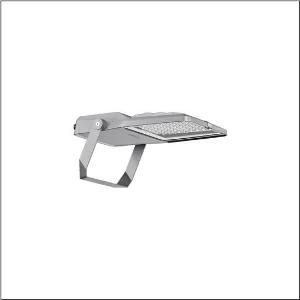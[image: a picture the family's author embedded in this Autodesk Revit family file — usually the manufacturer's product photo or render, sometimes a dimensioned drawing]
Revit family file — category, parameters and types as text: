
# Revit family: floodlight_fl_21_iq_mini___pl52_5xa7772d2d1a_b3d3
name_source: partatom
category: Lighting Fixtures
units: mm (PartAtom-declared; Revit-internal decimal feet)

## family parameters
Cut with Voids When Loaded = No
Host = Face
Light Source = No
Part Type = Normal
Room Calculation Point = No
Round Connector Dimension = Use Diameter
Shared = No

## types (1)
- --- (1 x LED, 17830 lm, 143 W, 3000K)
    Apparent Load = 143 VA
    CIE Flux Codes = 26 60 98 100 100
    Color Rendering = 70
    Color Temperature = 3000K
    Default Elevation = 1800 mm
    Description = Floodlight FL 21 iQ mini, floodlight, primary light control with lens, of PMMA, primary optical cover: protective disc, of toughened safety glass, transparent, light distribution: PL52, light emission: direct distribution, installation type: surface-mounted, LED, High Power LED, rated luminous flux: 17.830lm, luminous efficacy: 125lm/W, light colour: 730, colour temperature: 3000K, control: Street-Remote, Auto-Match, Temp-Guard, Night-Set, Smart-Wire, Desk-Remote (wireless, voltage-free reading and setting of iQ features in the workshop via application-optimized NFC function/RFID function), optimised constant luminous flux control (CLO 2.0), with terminal, 6-pole, mains connection: 220..240V, AC, 50/60Hz, start of lifetime: 143W, end of service life: 152W, reduction: 61W, luminaire housing, of diecast aluminium, powder-coated, Siteco® metallic grey (DB 702S), corrosivity category C5 mid according to DIN EN ISO 12944, sealing non-destructively replaceable, mounting bracket, of steel, galvanised, powder-coated, Siteco® metallic grey (DB 702S), protection rating (complete): IP66, insulation class (complete): insulation class II (safety insulation), certification: CE, ENEC, VDE, protection symbol: D, impact resistance: IK08, permissible operating ambient temperature: -40..+40°C, permissible operating ambient temperature for outdoor applications: -40..+50°C, standard: DIN EN 12944, LABS conformity tested according to VDMA 24364:2018-05, packaging unit: 1 piece

Light Distribution: PL52
    Height = 70 mm
    Lamp = 1 x LED
    Lamp Light Flux = 17830 lm
    Lamp Power = 143 W
    Lamp count = 1
    Length = 485 mm
    Luminous efficacy = 125 lm/W
    Manufacturer = Siteco
    ModVariant = No
    Model = 5XA7772D2D1A
    Number of Poles = 1
    OnlyDefault = Yes
    Power Factor = 1
    Product Name = Floodlight FL 21 iQ mini | PL52
    Product group = floodlight | pylon annexe
    ProductGroupID = 6200
    Protection Class = Protection class II
    Protection Degree = IP 66
    RLX_Detail_Level = 1
    RLX_Emergency_Light_Flux = 0 lm
    RLX_Emergency_Type = 0
    RLX_Emergency_Type_DB = No
    RlxData = <blob elided: 96733 chars, md5=5193b9d2>
    Socket = socket
    Standby Power = 0 W
    System Light Flux = 17830 lm
    System Power = 143 W
    Type Comments = factory setting: luminous flux: 100 % | dim-lin: 254 | 730 mA
    Type Image = l_1006845.jpg
    URL = http://relux.com
    VarID = @adj_096087
    Voltage = 0 V
    Weight = 0.00 kg
    Width = 337 mm

## geometry (parser evidence)
native form markers: Blend x4, Sweep x14
no freeform markers — native parametric forms only
